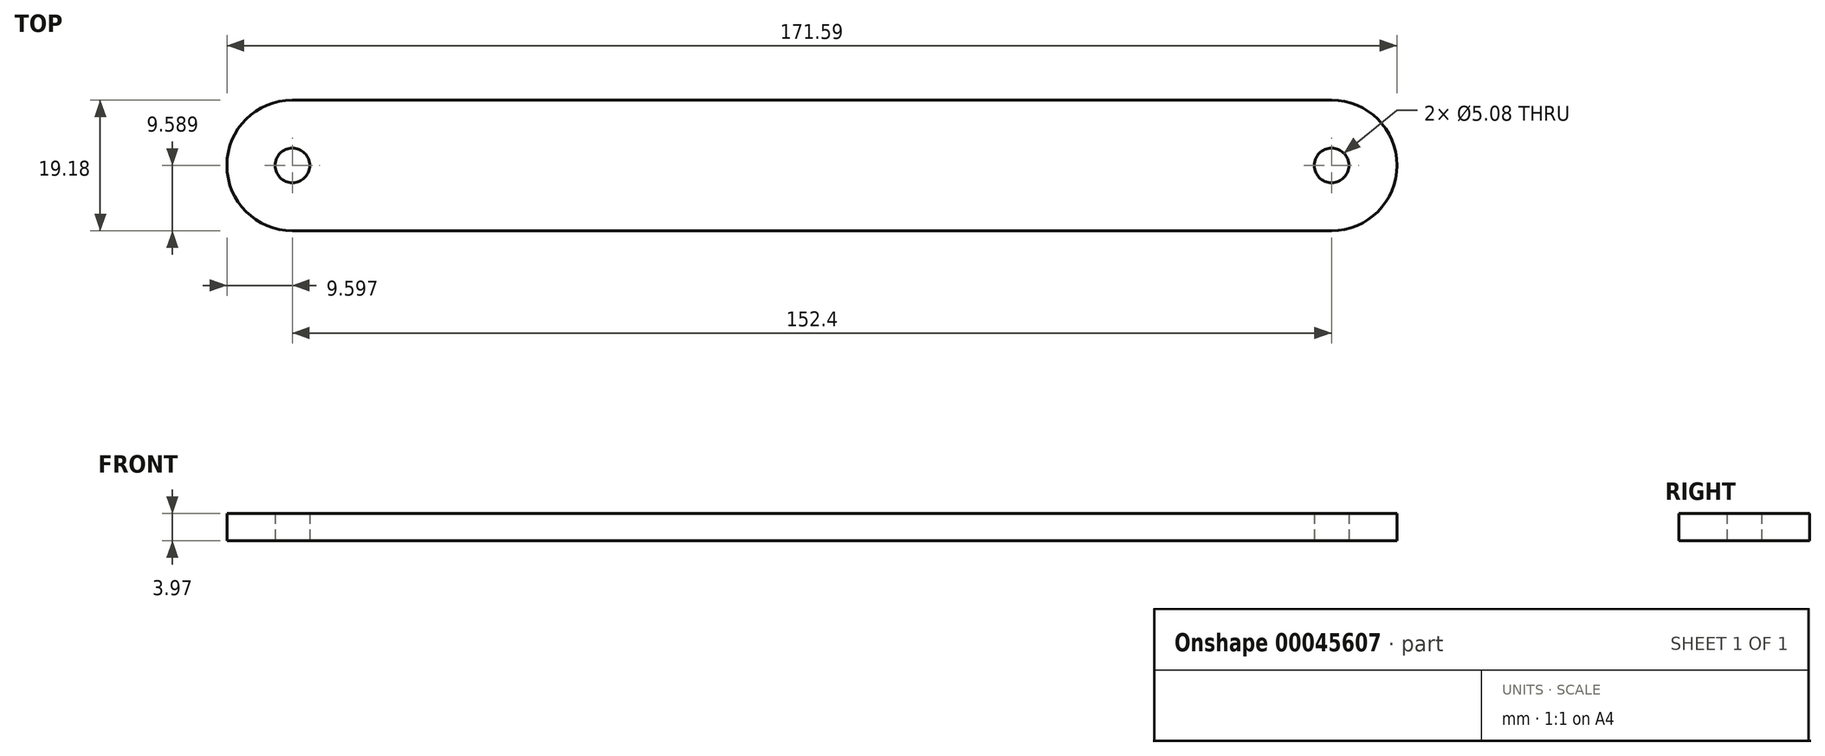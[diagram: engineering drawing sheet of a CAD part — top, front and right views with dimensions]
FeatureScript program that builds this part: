
annotation { "Feature Type Name" : "Feature", "Feature Type Description" : "" }
export const myFeature = defineFeature(function(context is Context, id is Id, definition is map)
    precondition{}
    {
        {
            var Q0;
            Q0=qCreatedBy(makeId("Top.planeOp"),FACE);
            var sketch = newSketch(context, id + "F0", { "sketchPlane" : qUnion([Q0])});
            skLineSegment(sketch, "E0.bottom", {"start": v(-20.57, 6.76) * mm, "end": v(131.83, 6.76) * mm});
            skLineSegment(sketch, "E0.top", {"start": v(-20.57, -12.42) * mm, "end": v(131.83, -12.42) * mm});
            skLineSegment(sketch, "E0.left", {"start": v(-20.57, -0.3) * mm, "end": v(-20.57, -5.37) * mm});
            skLineSegment(sketch, "E0.right", {"start": v(131.83, -0.3) * mm, "end": v(131.83, -5.37) * mm});
            skArc(sketch, "E1", {"start": v(-20.57, 6.76) * mm, "mid": v(-30.17, -2.83) * mm, "end": v(-20.57, -12.42) * mm});
            skArc(sketch, "E2", {"start": v(131.83, -12.42) * mm, "mid": v(141.42, -2.83) * mm, "end": v(131.83, 6.76) * mm});
            skCircle(sketch, "E3", {"center": v(131.83, -2.83) * mm, "radius": 2.54 * mm});
            skCircle(sketch, "E4", {"center": v(-20.57, -2.83) * mm, "radius": 2.54 * mm});
            skSolve(sketch);
        }
        {
            var Q0;
            Q0=makeQuery(id+"F0.imprint","IMPRINT",FACE,{"disambiguationData":[TD([[makeQuery(id+"F0.imprint","IMPRINT",EDGE,{"derivedFrom":sQuery(id+"F0.wireOp",EDGE,"E0.bottom")}),-1.0]])]});
            extrude(context, id + "F1", {"entities" : qUnion([Q0]), "depth" : 3.97 * mm});
        }
    });
